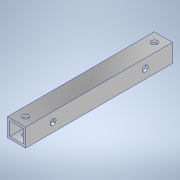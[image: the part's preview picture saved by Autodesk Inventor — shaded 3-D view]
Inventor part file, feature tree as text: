
AUTODESK INVENTOR PART (.ipt)
format: ipt  version: 2020.3 (Build 243373000, 373)  size: 130,048 bytes
history: native  units: mm
features: sketch x3, hole x2, other x1, extrude x1
ambient origin geometry x8: Origin, YZ Plane, XZ Plane, XY Plane, X Axis, Y Axis, Z Axis, Center Point
bodies: Body1 (feature_tree)
feature tree (7):
  other  "ソリッド1"
  extrude  "押し出し1"  Depth=9.0mm
  hole  "穴1"  [1 undecoded]
  hole  "穴2"  [1 undecoded]
  sketch  "スケッチ1"
  sketch  "スケッチ2"
  sketch  "スケッチ3"
note: 2 required parameter values undecoded (feature->parameter linkage not recoverable at this tier; creation-order binding heuristic only, values carry confidence <= 0.55)
